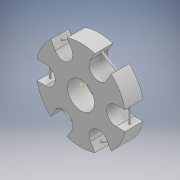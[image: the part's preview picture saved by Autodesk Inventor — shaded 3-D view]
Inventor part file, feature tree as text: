
AUTODESK INVENTOR PART (.ipt)
format: ipt  version: 2018 (Build 220112000, 112)  size: 190,976 bytes
history: native  units: mm
features: sketch x8, extrude x3, pattern_circular x2, plane x1, sweep x1, projected_geometry x1
ambient origin geometry x8: Origin, YZ Plane, XZ Plane, XY Plane, X Axis, Y Axis, Z Axis, Center Point
bodies: Solid1 (feature_tree)
feature tree (16):
  extrude  "Extrusion1"  Depth=20.0mm TaperAngle=0.0deg
  extrude  "Extrusion2"  Depth=20.0mm TaperAngle=0.0deg
  pattern_circular  "Circular Pattern1"  Count=6 Angle=360.0deg
  sketch  "Sketch3"  dims[d9=10.0mm d10=2.0mm]
  sketch  "Sketch4"  dims[d11=0.0mm d12=0.0mm d13=60.0mm d14=360.0deg]
  plane  "Work Plane1"
  sketch  "Sketch5"  dims[d16=30.0mm d17=10.0mm d18=0.0mm]
  sketch  "Sketch6"
  sweep  "Sweep1"
  pattern_circular  "Circular Pattern2"  Count=6 Angle=360.0deg
  extrude  "Extrusion3"  Depth=10.0mm TaperAngle=0.0deg
  sketch  "Sketch1"  dims[d0=100.0mm d1=20.0mm d2=0.0mm]
  sketch  "Sketch2"  dims[d3=21.0mm d4=20.0mm d5=0.0mm d6=60.0mm d7=360.0deg]
  projected_geometry  "Projected Loop1"
  sketch  "Sketch7"
  sketch  "Sketch8"
